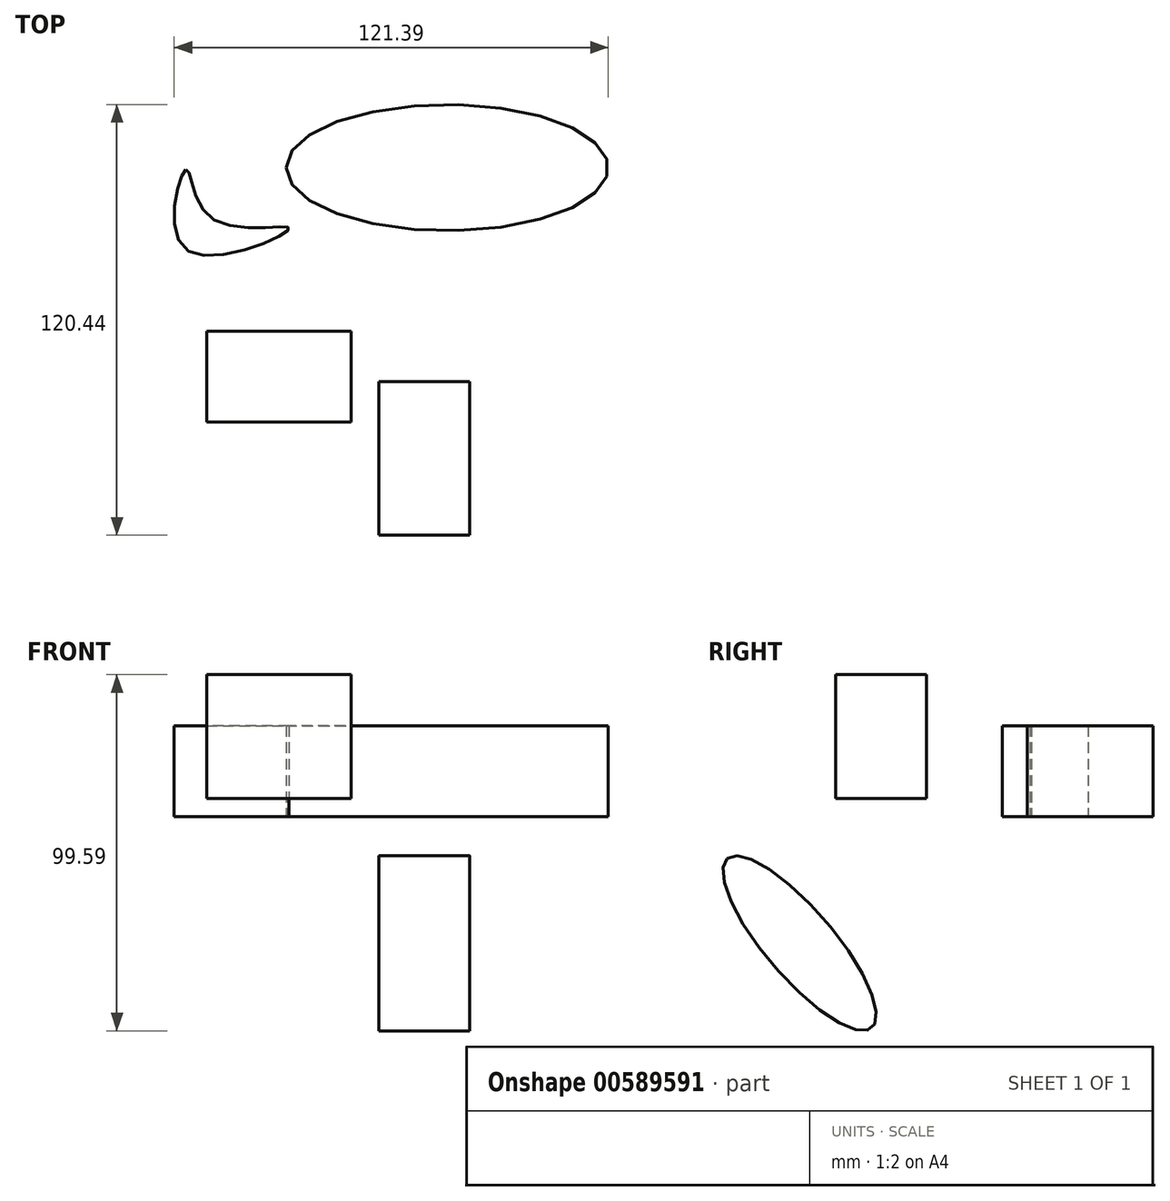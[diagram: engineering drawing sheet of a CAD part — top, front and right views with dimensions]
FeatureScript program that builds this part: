
annotation { "Feature Type Name" : "Feature", "Feature Type Description" : "" }
export const myFeature = defineFeature(function(context is Context, id is Id, definition is map)
    precondition{}
    {
        {
            var Q0;
            Q0=qCreatedBy(makeId("Front.planeOp"),FACE);
            var sketch = newSketch(context, id + "F0", { "sketchPlane" : qUnion([Q0])});
            skLineSegment(sketch, "E0.bottom", {"start": v(-48.24, 39.72) * mm, "end": v(-7.8, 39.72) * mm});
            skLineSegment(sketch, "E0.top", {"start": v(-48.24, 5.05) * mm, "end": v(-7.8, 5.05) * mm});
            skLineSegment(sketch, "E0.left", {"start": v(-48.24, 39.72) * mm, "end": v(-48.24, 5.05) * mm});
            skLineSegment(sketch, "E0.right", {"start": v(-7.8, 39.72) * mm, "end": v(-7.8, 5.05) * mm});
            skSolve(sketch);
        }
        {
            var Q0;
            Q0 = qSketchRegion(id + "F0", true);
            extrude(context, id + "F1", {"entities" : qUnion([Q0]), "depth" : 25.4 * mm, "offsetDistance" : 25.4 * mm});
        }
        {
            var Q0;
            Q0=qCreatedBy(makeId("Right.planeOp"),FACE);
            var sketch = newSketch(context, id + "F2", { "sketchPlane" : qUnion([Q0])});
            skEllipse(sketch, "E1", {"center": v(-35.53, -35.38) * mm, "majorRadius": 31.14 * mm, "minorRadius": 9.58 * mm, "majorAxis": v(-0.65, 0.76)});
            skSolve(sketch);
        }
        {
            var Q0;
            Q0 = qSketchRegion(id + "F2", true);
            extrude(context, id + "F3", {"entities" : qUnion([Q0]), "depth" : 25.4 * mm, "offsetDistance" : 25.4 * mm});
        }
        {
            var Q0;
            Q0=qCreatedBy(makeId("Top.planeOp"),FACE);
            var sketch = newSketch(context, id + "F4", { "sketchPlane" : qUnion([Q0])});
            skEllipse(sketch, "E2", {"center": v(19.06, 45.78) * mm, "majorRadius": 45.06 * mm, "minorRadius": 17.64 * mm, "majorAxis": v(-1, 0)});
            skSolve(sketch);
        }
        {
            var Q0;
            Q0 = qSketchRegion(id + "F4", true);
            extrude(context, id + "F5", {"entities" : qUnion([Q0]), "depth" : 25.4 * mm, "offsetDistance" : 25.4 * mm});
        }
        {
            var Q0;
            Q0=qCreatedBy(makeId("Top.planeOp"),FACE);
            var sketch = newSketch(context, id + "F6", { "sketchPlane" : qUnion([Q0])});
            skFitSpline(sketch, "E3", {"points": [v(-54.01, 45.2) * mm, v(-54.01, 22.96) * mm, v(-25.13, 28.74) * mm, v(-46.8, 31.63) * mm, v(-54.01, 45.2) * mm]});
            skSolve(sketch);
        }
        {
            var Q0;
            Q0 = qSketchRegion(id + "F6", true);
            extrude(context, id + "F7", {"entities" : qUnion([Q0]), "depth" : 25.4 * mm, "offsetDistance" : 25.4 * mm});
        }
    });
